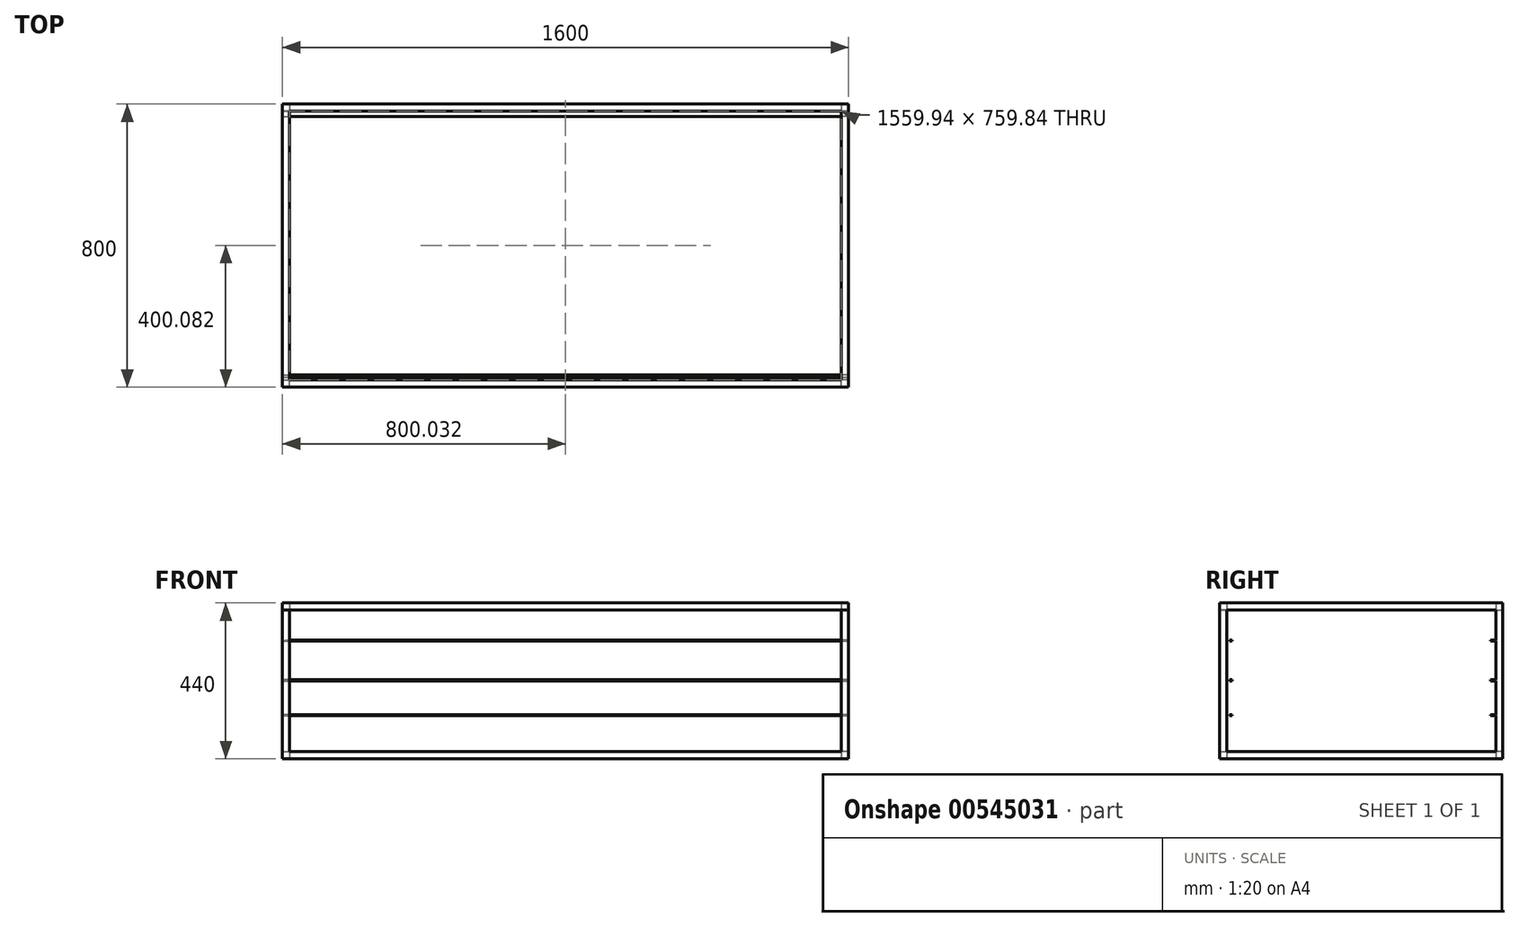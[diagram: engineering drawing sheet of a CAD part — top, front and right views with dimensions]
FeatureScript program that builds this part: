
annotation { "Feature Type Name" : "Feature", "Feature Type Description" : "" }
export const myFeature = defineFeature(function(context is Context, id is Id, definition is map)
    precondition{}
    {
        {
            var Q0;
            Q0=qCreatedBy(makeId("Top.planeOp"),FACE);
            var sketch = newSketch(context, id + "F0", { "sketchPlane" : qUnion([Q0])});
            skLineSegment(sketch, "E0.bottom", {"start": v(800, -400) * mm, "end": v(-800, -400) * mm});
            skLineSegment(sketch, "E0.top", {"start": v(800, 400) * mm, "end": v(-800, 400) * mm});
            skLineSegment(sketch, "E0.left", {"start": v(800, -400) * mm, "end": v(800, 400) * mm});
            skLineSegment(sketch, "E0.right", {"start": v(-800, -400) * mm, "end": v(-800, 400) * mm});
            skPoint(sketch, "E0.middle", {"position": v(0, 0) * mm});
            skLineSegment(sketch, "E1.0", {"start": v(780, -380) * mm, "end": v(-780, -380) * mm});
            skLineSegment(sketch, "E1.1", {"start": v(780, -380) * mm, "end": v(780, 380) * mm});
            skLineSegment(sketch, "E1.2", {"start": v(780, 380) * mm, "end": v(-780, 380) * mm});
            skLineSegment(sketch, "E1.3", {"start": v(-780, -380) * mm, "end": v(-780, 380) * mm});
            skSolve(sketch);
        }
        {
            var Q0;
            Q0 = qSketchRegion(id + "F0", true);
            extrude(context, id + "F1", {"entities" : qUnion([Q0]), "depth" : 20 * mm, "offsetDistance" : 25 * mm});
        }
        {
            var Q0;
            Q0=makeQuery(id+"F1.opExtrude","CAP_FACE",FACE,{"disambiguationData":[OSD([sQuery(id+"F0.wireOp",EDGE,"E0.bottom"),sQuery(id+"F0.wireOp",EDGE,"E0.top"),sQuery(id+"F0.wireOp",EDGE,"E0.left"),sQuery(id+"F0.wireOp",EDGE,"E0.right"),sQuery(id+"F0.wireOp",EDGE,"E1.0"),sQuery(id+"F0.wireOp",EDGE,"E1.1"),sQuery(id+"F0.wireOp",EDGE,"E1.2"),sQuery(id+"F0.wireOp",EDGE,"E1.3")])],"isStart":false});
            var sketch = newSketch(context, id + "F2", { "sketchPlane" : qUnion([Q0])});
            skLineSegment(sketch, "E2.bottom", {"start": v(800, -400) * mm, "end": v(780, -400) * mm});
            skLineSegment(sketch, "E2.top", {"start": v(800, -380) * mm, "end": v(780, -380) * mm});
            skLineSegment(sketch, "E2.left", {"start": v(800, -400) * mm, "end": v(800, -380) * mm});
            skLineSegment(sketch, "E2.right", {"start": v(780, -400) * mm, "end": v(780, -380) * mm});
            skLineSegment(sketch, "E3.bottom", {"start": v(800, 400) * mm, "end": v(780, 400) * mm});
            skLineSegment(sketch, "E3.top", {"start": v(800, 380) * mm, "end": v(780, 380) * mm});
            skLineSegment(sketch, "E3.left", {"start": v(800, 400) * mm, "end": v(800, 380) * mm});
            skLineSegment(sketch, "E3.right", {"start": v(780, 400) * mm, "end": v(780, 380) * mm});
            skLineSegment(sketch, "E4.bottom", {"start": v(-800, 400) * mm, "end": v(-780, 400) * mm});
            skLineSegment(sketch, "E4.top", {"start": v(-800, 380) * mm, "end": v(-780, 380) * mm});
            skLineSegment(sketch, "E4.left", {"start": v(-800, 400) * mm, "end": v(-800, 380) * mm});
            skLineSegment(sketch, "E4.right", {"start": v(-780, 400) * mm, "end": v(-780, 380) * mm});
            skLineSegment(sketch, "E5.bottom", {"start": v(-800, -400) * mm, "end": v(-780, -400) * mm});
            skLineSegment(sketch, "E5.top", {"start": v(-800, -380) * mm, "end": v(-780, -380) * mm});
            skLineSegment(sketch, "E5.left", {"start": v(-800, -400) * mm, "end": v(-800, -380) * mm});
            skLineSegment(sketch, "E5.right", {"start": v(-780, -400) * mm, "end": v(-780, -380) * mm});
            skSolve(sketch);
        }
        {
            var Q0;
            Q0 = qSketchRegion(id + "F2", true);
            extrude(context, id + "F3", {"entities" : qUnion([Q0]), "operationType" : NewBodyOperationType.ADD, "depth" : 400 * mm, "offsetDistance" : 25 * mm});
        }
        {
            var Q0;
            Q0=makeQuery(id+"F3.opExtrude","CAP_FACE",FACE,{"disambiguationData":[OSD([sQuery(id+"F2.wireOp",EDGE,"E3.bottom"),sQuery(id+"F2.wireOp",EDGE,"E3.top"),sQuery(id+"F2.wireOp",EDGE,"E3.left"),sQuery(id+"F2.wireOp",EDGE,"E3.right")])],"isStart":false});
            var sketch = newSketch(context, id + "F4", { "sketchPlane" : qUnion([Q0])});
            skLineSegment(sketch, "E6.bottom", {"start": v(800, 400) * mm, "end": v(-799.94, 400) * mm});
            skLineSegment(sketch, "E6.top", {"start": v(800, -399.84) * mm, "end": v(-799.94, -399.84) * mm});
            skLineSegment(sketch, "E6.left", {"start": v(800, 400) * mm, "end": v(800, -399.84) * mm});
            skLineSegment(sketch, "E6.right", {"start": v(-799.94, 400) * mm, "end": v(-799.94, -399.84) * mm});
            skLineSegment(sketch, "E7.0", {"start": v(780, -379.84) * mm, "end": v(-779.94, -379.84) * mm});
            skLineSegment(sketch, "E7.1", {"start": v(780, 380) * mm, "end": v(780, -379.84) * mm});
            skLineSegment(sketch, "E7.2", {"start": v(780, 380) * mm, "end": v(-779.94, 380) * mm});
            skLineSegment(sketch, "E7.3", {"start": v(-779.94, 380) * mm, "end": v(-779.94, -379.84) * mm});
            skSolve(sketch);
        }
        {
            var Q0;
            Q0 = qSketchRegion(id + "F4", true);
            extrude(context, id + "F5", {"entities" : qUnion([Q0]), "operationType" : NewBodyOperationType.ADD, "depth" : 20 * mm, "offsetDistance" : 25 * mm});
        }
        {
            var Q0;
            Q0=makeQuery(id+"F3.opExtrude","SWEPT_FACE",FACE,{"disambiguationData":[OSD([sQuery(id+"F2.wireOp",EDGE,"E3.top")])]});
            var sketch = newSketch(context, id + "F6", { "sketchPlane" : qUnion([Q0])});
            skLineSegment(sketch, "E8", {"start": v(800, 121.17) * mm, "end": v(-799.94, 121.17) * mm});
            skLineSegment(sketch, "E9", {"start": v(-799.94, 220) * mm, "end": v(800, 220) * mm});
            skLineSegment(sketch, "E10", {"start": v(800, 331.97) * mm, "end": v(-799.94, 331.97) * mm});
            skLineSegment(sketch, "E11.0", {"start": v(800, 334.97) * mm, "end": v(-783.19, 334.97) * mm});
            skLineSegment(sketch, "E12.0", {"start": v(-799.94, 223) * mm, "end": v(800, 223) * mm});
            skLineSegment(sketch, "E13.0", {"start": v(800, 124.17) * mm, "end": v(-799.94, 124.17) * mm});
            skLineSegment(sketch, "E14", {"start": v(800, 334.97) * mm, "end": v(800, 331.97) * mm});
            skLineSegment(sketch, "E15", {"start": v(800, 223) * mm, "end": v(800, 220) * mm});
            skLineSegment(sketch, "E16", {"start": v(-783.19, 334.97) * mm, "end": v(-799.94, 331.97) * mm});
            skLineSegment(sketch, "E17", {"start": v(-799.94, 223) * mm, "end": v(-799.94, 220) * mm});
            skLineSegment(sketch, "E18", {"start": v(-799.94, 124.17) * mm, "end": v(-799.94, 121.17) * mm});
            skLineSegment(sketch, "E19", {"start": v(800, 124.17) * mm, "end": v(800, 121.17) * mm});
            skSolve(sketch);
        }
        {
            var Q0;
            {var subQ0=sQuery(id+"F6.wireOp",EDGE,"E16");Q0=makeQuery(id+"F6.imprint","IMPRINT",FACE,{"disambiguationData":[TD([[makeQuery(id+"F6.imprint","IMPRINT",EDGE,{"derivedFrom":subQ0}),1.0]])]});}
            var Q1;
            {var subQ0=sQuery(id+"F6.wireOp",EDGE,"E14");Q1=makeQuery(id+"F6.imprint","IMPRINT",FACE,{"disambiguationData":[TD([[makeQuery(id+"F6.imprint","IMPRINT",EDGE,{"derivedFrom":subQ0}),-1.0]])]});}
            var Q2;
            {var subQ0=sQuery(id+"F6.wireOp",EDGE,"E17");Q2=makeQuery(id+"F6.imprint","IMPRINT",FACE,{"disambiguationData":[TD([[makeQuery(id+"F6.imprint","IMPRINT",EDGE,{"derivedFrom":subQ0}),1.0]])]});}
            var Q3;
            {var subQ0=sQuery(id+"F6.wireOp",EDGE,"E15");Q3=makeQuery(id+"F6.imprint","IMPRINT",FACE,{"disambiguationData":[TD([[makeQuery(id+"F6.imprint","IMPRINT",EDGE,{"derivedFrom":subQ0}),-1.0]])]});}
            var Q4;
            {var subQ0=sQuery(id+"F6.wireOp",EDGE,"E8");var subQ1=sQuery(id+"F2.wireOp",EDGE,"E3.top");var subQ2=makeQuery(id+"F3.opExtrude","SWEPT_EDGE",EDGE,{"disambiguationData":[OSD([sQuery(id+"F0.wireOp",EDGE,"E0.left"),subQ1,sQuery(id+"F2.wireOp",EDGE,"E3.left")])]});var subQ3=makeQuery(id+"F6.imprint","INTERSECT",VERTEX,{"derivedFrom":[subQ2,subQ0]});Q4=makeQuery(id+"F6.imprint","IMPRINT",FACE,{"disambiguationData":[TD([[makeQuery(id+"F6.imprint","IMPRINT",EDGE,{"disambiguationData":[TD([[subQ3,-1.0]])],"derivedFrom":subQ0}),-1.0]])]});}
            var Q5;
            {var subQ0=sQuery(id+"F6.wireOp",EDGE,"E18");Q5=makeQuery(id+"F6.imprint","IMPRINT",FACE,{"disambiguationData":[TD([[makeQuery(id+"F6.imprint","IMPRINT",EDGE,{"derivedFrom":subQ0}),1.0]])]});}
            extrude(context, id + "F7", {"entities" : qUnion([Q0, Q1, Q2, Q3, Q4, Q5]), "operationType" : NewBodyOperationType.ADD, "depth" : 753 * mm, "offsetDistance" : 25 * mm});
        }
        {
            var Q0;
            Q0=makeQuery(id+"F3.opExtrude","SWEPT_FACE",FACE,{"disambiguationData":[OSD([sQuery(id+"F2.wireOp",EDGE,"E2.top")])]});
            var sketch = newSketch(context, id + "F8", { "sketchPlane" : qUnion([Q0])});
            skLineSegment(sketch, "E20.bottom", {"start": v(-800, 126.87) * mm, "end": v(501.35, 126.87) * mm});
            skLineSegment(sketch, "E20.top", {"start": v(-800, 133.98) * mm, "end": v(501.35, 133.98) * mm});
            skLineSegment(sketch, "E20.left", {"start": v(-800, 126.87) * mm, "end": v(-800, 133.98) * mm});
            skLineSegment(sketch, "E20.right", {"start": v(501.35, 126.87) * mm, "end": v(501.35, 133.98) * mm});
            skLineSegment(sketch, "E21.bottom", {"start": v(650.86, 243.64) * mm, "end": v(-800, 243.64) * mm});
            skLineSegment(sketch, "E21.top", {"start": v(650.86, 220) * mm, "end": v(-800, 220) * mm});
            skLineSegment(sketch, "E21.left", {"start": v(650.86, 243.64) * mm, "end": v(650.86, 220) * mm});
            skLineSegment(sketch, "E21.right", {"start": v(-800, 243.64) * mm, "end": v(-800, 220) * mm});
            skLineSegment(sketch, "E22.bottom", {"start": v(-780, 344.95) * mm, "end": v(501.92, 344.95) * mm});
            skLineSegment(sketch, "E22.top", {"start": v(-780, 323.74) * mm, "end": v(501.92, 323.74) * mm});
            skLineSegment(sketch, "E22.left", {"start": v(-780, 344.95) * mm, "end": v(-780, 323.74) * mm});
            skLineSegment(sketch, "E22.right", {"start": v(501.92, 344.95) * mm, "end": v(501.92, 323.74) * mm});
            skSolve(sketch);
        }
        {
            var Q0;
            Q0=makeQuery(id+"F7.opExtrude","SWEPT_FACE",FACE,{"disambiguationData":[OSD([sQuery(id+"F6.wireOp",EDGE,"E11.0")])]});
            var sketch = newSketch(context, id + "F9", { "sketchPlane" : qUnion([Q0])});
            skLineSegment(sketch, "E23.bottom", {"start": v(1474.65, -365) * mm, "end": v(-1051, -365) * mm});
            skLineSegment(sketch, "E23.top", {"start": v(1474.65, 365) * mm, "end": v(-1051, 365) * mm});
            skLineSegment(sketch, "E23.left", {"start": v(1474.65, -365) * mm, "end": v(1474.65, 365) * mm});
            skLineSegment(sketch, "E23.right", {"start": v(-1051, -365) * mm, "end": v(-1051, 365) * mm});
            skSolve(sketch);
        }
        {
            var Q0;
            Q0=makeQuery(id+"F9.imprint","IMPRINT",FACE,{"disambiguationData":[TD([[makeQuery(id+"F9.imprint","IMPRINT",EDGE,{"derivedFrom":sQuery(id+"F9.wireOp",EDGE,"E23.bottom")}),-1.0]])]});
            extrude(context, id + "F10", {"entities" : qUnion([Q0]), "operationType" : NewBodyOperationType.REMOVE, "oppositeDirection" : true, "depth" : 245 * mm, "offsetDistance" : 25 * mm});
        }
    });
